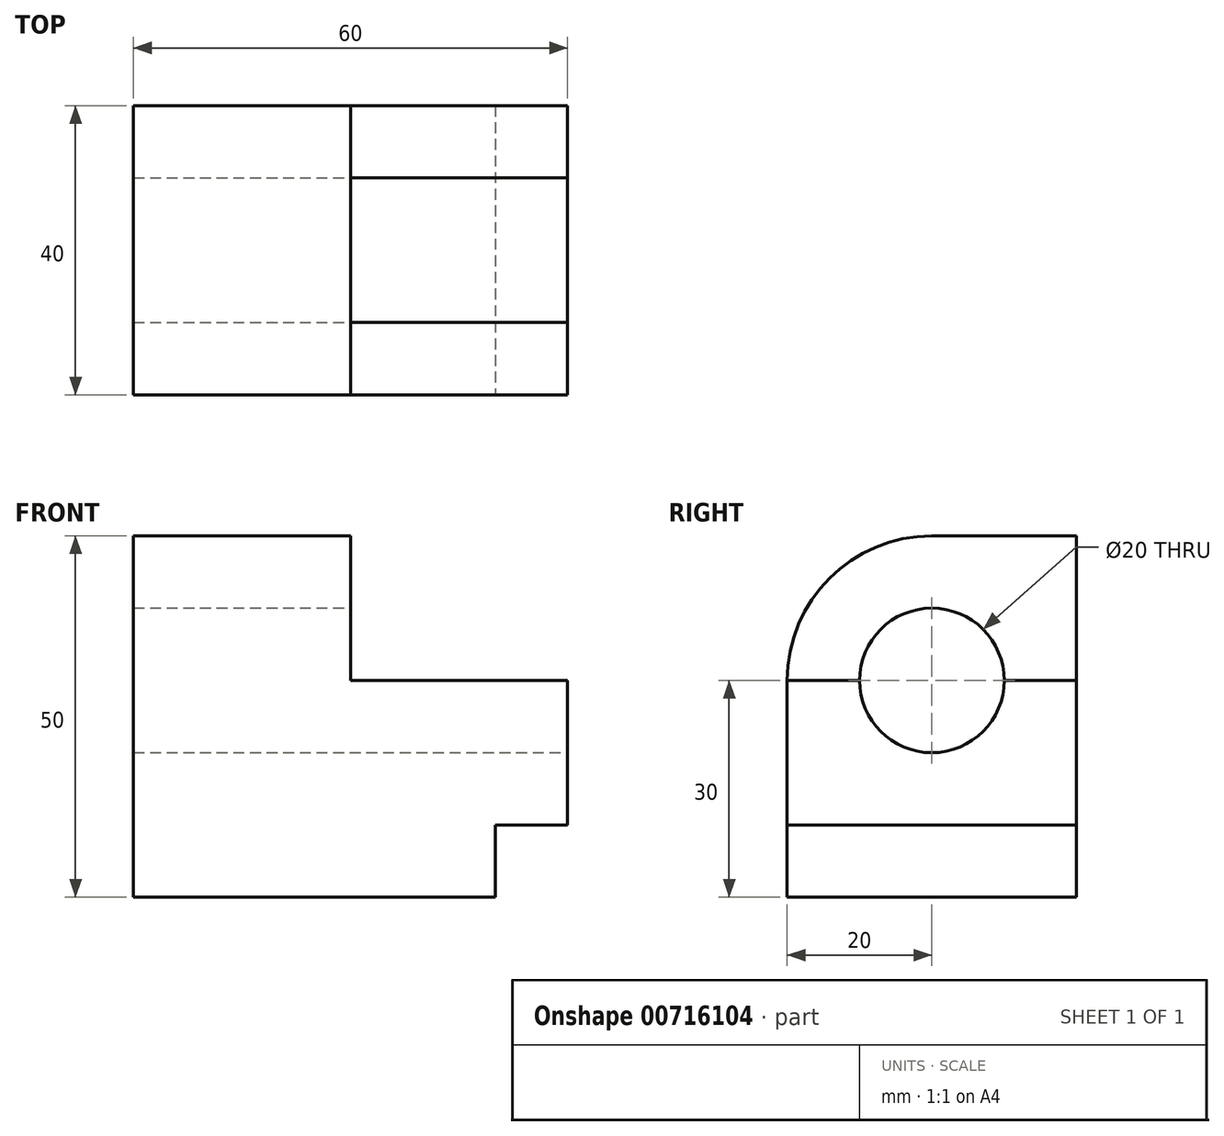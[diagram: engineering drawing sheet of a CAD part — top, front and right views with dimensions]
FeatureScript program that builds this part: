
annotation { "Feature Type Name" : "Feature", "Feature Type Description" : "" }
export const myFeature = defineFeature(function(context is Context, id is Id, definition is map)
    precondition{}
    {
        {
            var Q0;
            Q0=qCreatedBy(makeId("Right.planeOp"),FACE);
            var sketch = newSketch(context, id + "F0", { "sketchPlane" : qUnion([Q0])});
            skLineSegment(sketch, "E0.bottom", {"start": v(0, 0) * mm, "end": v(40, 0) * mm});
            skLineSegment(sketch, "E0.top", {"start": v(0, 50) * mm, "end": v(40, 50) * mm});
            skLineSegment(sketch, "E0.left", {"start": v(0, 0) * mm, "end": v(0, 50) * mm});
            skLineSegment(sketch, "E0.right", {"start": v(40, 0) * mm, "end": v(40, 50) * mm});
            skSolve(sketch);
        }
        {
            var Q0;
            Q0 = qSketchRegion(id + "F0", true);
            extrude(context, id + "F1", {"entities" : qUnion([Q0]), "depth" : 60 * mm, "offsetDistance" : 25 * mm});
        }
        {
            var Q0;
            Q0=makeQuery(id+"F1.opExtrude","CAP_FACE",FACE,{"disambiguationData":[OSD([sQuery(id+"F0.wireOp",EDGE,"E0.bottom"),sQuery(id+"F0.wireOp",EDGE,"E0.top"),sQuery(id+"F0.wireOp",EDGE,"E0.left"),sQuery(id+"F0.wireOp",EDGE,"E0.right")])],"isStart":false});
            var sketch = newSketch(context, id + "F2", { "sketchPlane" : qUnion([Q0])});
            skLineSegment(sketch, "E1.bottom", {"start": v(40, 50) * mm, "end": v(0, 50) * mm});
            skLineSegment(sketch, "E1.top", {"start": v(40, 30) * mm, "end": v(0, 30) * mm});
            skLineSegment(sketch, "E1.left", {"start": v(40, 50) * mm, "end": v(40, 30) * mm});
            skLineSegment(sketch, "E1.right", {"start": v(0, 50) * mm, "end": v(0, 30) * mm});
            skSolve(sketch);
        }
        {
            var Q0;
            Q0 = qSketchRegion(id + "F2", true);
            extrude(context, id + "F3", {"entities" : qUnion([Q0]), "operationType" : NewBodyOperationType.REMOVE, "oppositeDirection" : true, "depth" : 30 * mm, "offsetDistance" : 25 * mm});
        }
        {
            var Q0;
            Q0=makeQuery(id+"F1.opExtrude","CAP_FACE",FACE,{"disambiguationData":[OSD([sQuery(id+"F0.wireOp",EDGE,"E0.bottom"),sQuery(id+"F0.wireOp",EDGE,"E0.top"),sQuery(id+"F0.wireOp",EDGE,"E0.left"),sQuery(id+"F0.wireOp",EDGE,"E0.right")])],"isStart":false});
            var sketch = newSketch(context, id + "F4", { "sketchPlane" : qUnion([Q0])});
            skCircle(sketch, "E2", {"center": v(20, 30) * mm, "radius": 10 * mm});
            skSolve(sketch);
        }
        {
            var Q0;
            {var subQ0=sQuery(id+"F4.wireOp",EDGE,"E2");var subQ1=makeQuery(id+"F3.boolean.opBoolean","COPY",EDGE,{"derivedFrom":makeQuery(id+"F3.opExtrude","CAP_EDGE",EDGE,{"disambiguationData":[OSD([sQuery(id+"F2.wireOp",EDGE,"E1.top")])],"isStart":true})});var subQ2=makeQuery(id+"F4.imprint","INTERSECT",VERTEX,{"disambiguationData":[OD(0.0)],"derivedFrom":[subQ1,subQ0]});Q0=makeQuery(id+"F4.imprint","IMPRINT",FACE,{"disambiguationData":[TD([[makeQuery(id+"F4.imprint","IMPRINT",EDGE,{"disambiguationData":[TD([[subQ2,1.0]])],"derivedFrom":subQ0}),1.0]])]});}
            var Q1;
            {var subQ0=sQuery(id+"F4.wireOp",EDGE,"E2");var subQ1=makeQuery(id+"F3.boolean.opBoolean","COPY",EDGE,{"derivedFrom":makeQuery(id+"F3.opExtrude","CAP_EDGE",EDGE,{"disambiguationData":[OSD([sQuery(id+"F2.wireOp",EDGE,"E1.top")])],"isStart":true})});var subQ2=makeQuery(id+"F4.imprint","INTERSECT",VERTEX,{"disambiguationData":[OD(0.0)],"derivedFrom":[subQ1,subQ0]});Q1=makeQuery(id+"F4.imprint","IMPRINT",FACE,{"disambiguationData":[TD([[makeQuery(id+"F4.imprint","IMPRINT",EDGE,{"disambiguationData":[TD([[subQ2,-1.0]])],"derivedFrom":subQ0}),1.0]])]});}
            extrude(context, id + "F5", {"entities" : qUnion([Q0, Q1]), "operationType" : NewBodyOperationType.REMOVE, "endBound" : BoundingType.THROUGH_ALL, "oppositeDirection" : true, "depth" : 25 * mm, "offsetDistance" : 25 * mm});
        }
        {
            var Q0;
            Q0=makeQuery(id+"F1.opExtrude","SWEPT_FACE",FACE,{"disambiguationData":[OSD([sQuery(id+"F0.wireOp",EDGE,"E0.left")])]});
            var sketch = newSketch(context, id + "F6", { "sketchPlane" : qUnion([Q0])});
            skLineSegment(sketch, "E3.bottom", {"start": v(60, 0) * mm, "end": v(50, 0) * mm});
            skLineSegment(sketch, "E3.top", {"start": v(60, 10) * mm, "end": v(50, 10) * mm});
            skLineSegment(sketch, "E3.left", {"start": v(60, 0) * mm, "end": v(60, 10) * mm});
            skLineSegment(sketch, "E3.right", {"start": v(50, 0) * mm, "end": v(50, 10) * mm});
            skSolve(sketch);
        }
        {
            var Q0;
            Q0 = qSketchRegion(id + "F6", true);
            var Q1;
            Q1=makeQuery(id+"F6.imprint","IMPRINT",FACE,{"disambiguationData":[TD([[makeQuery(id+"F6.imprint","IMPRINT",EDGE,{"derivedFrom":sQuery(id+"F6.wireOp",EDGE,"E3.bottom")}),-1.0]])]});
            extrude(context, id + "F7", {"entities" : qUnion([Q0, Q1]), "operationType" : NewBodyOperationType.REMOVE, "endBound" : BoundingType.THROUGH_ALL, "oppositeDirection" : true, "depth" : 25 * mm, "offsetDistance" : 25 * mm});
        }
        {
            var Q0;
            Q0=makeQuery(id+"F1.opExtrude","SWEPT_EDGE",EDGE,{"disambiguationData":[OSD([sQuery(id+"F0.wireOp",EDGE,"E0.top"),sQuery(id+"F0.wireOp",EDGE,"E0.left")])]});
            fillet(context, id + "F8", {"entities" : qUnion([Q0]), "radius" : 20 * mm, "tangentPropagation" : true, "allowEdgeOverflow" : false});
        }
    });
